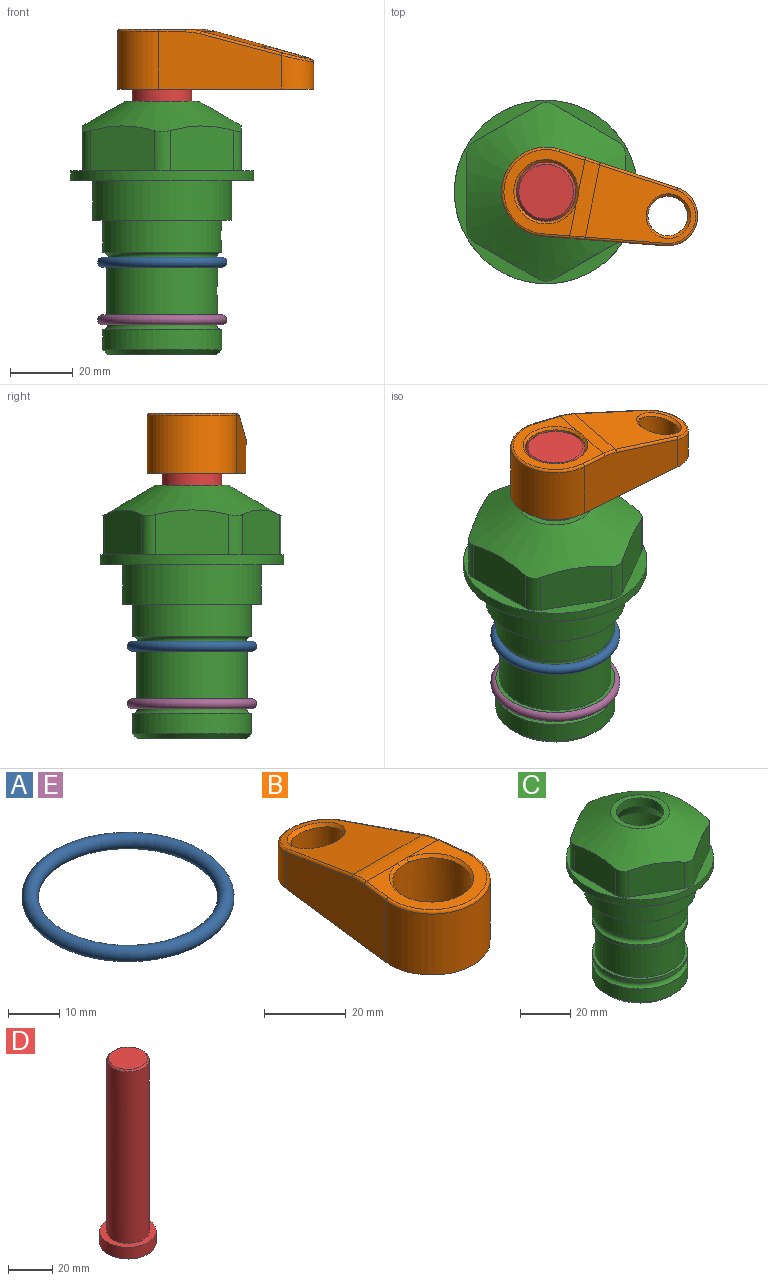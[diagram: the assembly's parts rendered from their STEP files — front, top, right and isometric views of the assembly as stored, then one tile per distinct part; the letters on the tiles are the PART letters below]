
ASSEMBLY  parts=5 mates=4
PART A: 1 faces, bbox 44.7x44.7x3.2 mm
  f0: torus R=19.05mm, axis (0,0,1), area 1193.9mm2
PART B: 31 faces, bbox 31.7x65.5x19.8 mm
  f0: plane 39.12x18.26mm, normal (0.99,0.12,0), area 612.2mm2, adj f1,f4,f7,f11,f13,f15
  f1: cylinder r=9.53mm len=18.91mm, axis (0,0,-1), area 296.1mm2, adj f0,f2,f7,f17
  f2: plane 39.12x18.26mm, normal (-0.99,0.12,0), area 612.2mm2, adj f1,f4,f7,f12,f14,f16
  f3: cylinder r=6.35mm len=12.7mm, axis (0,0,-1), area 362.4mm2, adj f7,f18
  f4: cylinder r=14.29mm len=28.58mm, axis (0,0,-1), area 882.2mm2, adj f0,f2,f7,f10
  f5: cylinder r=9.53mm len=19.05mm, axis (0,0,-1), area 1092.6mm2, adj f7,f19,f20
  f6: plane 26.99x23.69mm, normal (0,0,1), area 216.2mm2, adj f9,f10,f11,f12,f19
  f7: plane 63.5x28.58mm, normal (0,0,-1), area 661.8mm2, adj f0,f1,f2,f3,f4,f5,f22,f23
  f8: plane 33.52x23.6mm, normal (0,0.26,0.97), area 486mm2, adj f9,f15,f16,f17,f18
  f9: cylinder r=19.05mm len=24.72mm, axis (1,0,0), area 120.4mm2, adj f6,f8,f13,f14,f20
  f10: torus R=13.49mm, axis (0,0,1), area 59mm2, adj f4,f6,f11,f12
  f11: cylinder r=0.79mm len=8.67mm, axis (0.12,-0.99,0), area 10.8mm2, adj f0,f6,f10,f13
  f12: cylinder r=0.79mm len=8.67mm, axis (0.12,0.99,0), area 10.8mm2, adj f2,f6,f10,f14
  f13: bspline ~4.95x1.42mm, area 6.1mm2, adj f0,f9,f11,f15
  f14: bspline ~4.95x1.42mm, area 6.1mm2, adj f2,f9,f12,f16
  f15: cylinder r=0.79mm len=25.95mm, axis (0.12,-0.96,0.26), area 32.9mm2, adj f0,f8,f13,f17
  f16: cylinder r=0.79mm len=25.95mm, axis (0.12,0.96,-0.26), area 32.9mm2, adj f2,f8,f14,f17
  f17: bspline ~18.91x8.38mm, area 30mm2, adj f1,f8,f15,f16
  f18: bspline ~14.29x14.29mm, area 48.3mm2, adj f3,f8
  f19: cone r=9.53mm half-angle=45deg, axis (0,0,1), area 66.5mm2, adj f5,f6,f20
  f20: bspline ~3.22x0.96mm, area 3.5mm2, adj f5,f9,f19
  f21: plane 2.75x2.72mm, normal (0,0,-1), area 2.9mm2, adj f23,f25,f28
  f22: plane 23.05x15.88mm, normal (-0.99,-0.12,0), area 323.6mm2, adj f7,f25,f26,f27,f28,f29
  f23: plane 23.05x15.88mm, normal (0.99,-0.12,0), area 323.6mm2, adj f7,f21,f25,f27,f28,f30
  f24: cylinder r=9.53mm len=10.69mm, axis (0,0,-1), area 114.7mm2, adj f7,f27,f29,f30
  f25: cylinder r=12.7mm len=20.59mm, axis (0,0,-1), area 381.1mm2, adj f7,f21,f22,f23,f26,f28
  f26: plane 2.75x2.72mm, normal (0,0,-1), area 2.9mm2, adj f22,f25,f28
  f27: plane 19.72x18.37mm, normal (0,-0.26,-0.97), area 291.8mm2, adj f22,f23,f24,f28,f29,f30
  f28: cylinder r=15.88mm len=19.92mm, axis (1,0,0), area 54.8mm2, adj f21,f22,f23,f25,f26,f27
  f29: cylinder r=1.59mm len=11mm, axis (0,0,-1), area 34.7mm2, adj f7,f22,f24,f27
  f30: cylinder r=1.59mm len=11mm, axis (0,0,-1), area 34.7mm2, adj f7,f23,f24,f27
PART C: 36 faces, bbox 58.7x58.7x81 mm
  f0: cylinder r=17.78mm len=35.56mm, axis (0,0,1), area 1670.8mm2, adj f23,f24,f31
  f1: cylinder r=19.05mm len=38.1mm, axis (0,0,1), area 1191.9mm2, adj f26,f27,f30
  f2: plane 58.66x58.66mm, normal (0,0,-1), area 1150.6mm2, adj f3,f28
  f3: cylinder r=29.33mm len=58.66mm, axis (0,0,-1), area 585.1mm2, adj f2,f4
  f4: plane 58.66x58.66mm, normal (0,0,1), area 475.9mm2, adj f3,f5,f6,f7,f8,f9,f10,f11
  f5: plane 20.32x14.34mm, normal (-0.5,0.87,0), area 324.4mm2, adj f4,f15,f16,f17
  f6: plane 20.32x14.34mm, normal (0.5,0.87,0), area 324.4mm2, adj f4,f14,f15,f17
  f7: plane 23.48x14.34mm, normal (1,0,0), area 324.4mm2, adj f4,f13,f14,f17
  f8: plane 20.32x14.34mm, normal (0.5,-0.87,0), area 324.4mm2, adj f4,f12,f13,f17
  f9: plane 20.32x14.34mm, normal (-0.5,-0.87,0), area 324.4mm2, adj f4,f11,f12,f17
  f10: plane 23.48x14.34mm, normal (-1,0,0), area 324.4mm2, adj f4,f11,f16,f17
  f11: cylinder r=5.08mm len=12.85mm, axis (0,0,-1), area 67.2mm2, adj f4,f9,f10,f17
  f12: cylinder r=5.08mm len=12.85mm, axis (0,0,-1), area 67.2mm2, adj f4,f8,f9,f17
  f13: cylinder r=5.08mm len=12.85mm, axis (0,0,-1), area 67.2mm2, adj f4,f7,f8,f17
  f14: cylinder r=5.08mm len=12.85mm, axis (0,0,-1), area 67.2mm2, adj f4,f6,f7,f17
  f15: cylinder r=5.08mm len=12.85mm, axis (0,0,-1), area 67.2mm2, adj f4,f5,f6,f17
  f16: cylinder r=5.08mm len=12.85mm, axis (0,0,-1), area 67.2mm2, adj f4,f5,f10,f17
  f17: cone r=11.73mm half-angle=60deg, axis (0,0,-1), area 2071.8mm2, adj f5,f6,f7,f8,f9,f10,f11,f12
  f18: plane 23.46x23.46mm, normal (0,0,1), area 147.4mm2, adj f17,f35
  f19: plane 34.93x34.93mm, normal (0,0,-1), area 958mm2, adj f29
  f20: cylinder r=19.05mm len=38.1mm, axis (0,0,1), area 760.1mm2, adj f21,f29
  f21: torus R=19.05mm, axis (0,0,1), area 565.3mm2, adj f20,f22
  f22: cylinder r=19.05mm len=38.1mm, axis (0,0,1), area 190mm2, adj f21,f23
  f23: plane 38.1x38.1mm, normal (0,0,1), area 146.9mm2, adj f0,f22
  f24: plane 38.1x38.1mm, normal (0,0,-1), area 146.9mm2, adj f0,f25
  f25: cylinder r=19.05mm len=38.1mm, axis (0,0,1), area 190mm2, adj f24,f26
  f26: torus R=19.05mm, axis (0,0,1), area 565.3mm2, adj f1,f25
  f27: plane 44.45x44.45mm, normal (0,0,-1), area 411.7mm2, adj f1,f28
  f28: cylinder r=22.23mm len=44.45mm, axis (0,0,1), area 1773.5mm2, adj f2,f27
  f29: cone r=19.05mm half-angle=45deg, axis (0,0,1), area 257.5mm2, adj f19,f20
  f30: cylinder r=3.17mm len=6.75mm, axis (-1,0,0), area 128mm2, adj f1,f33
  f31: cylinder r=3.17mm len=6.35mm, axis (-1,0,0), area 102.5mm2, adj f0,f33
  f32: plane 25.4x25.4mm, normal (0,0,1), area 506.7mm2, adj f33
  f33: cylinder r=12.7mm len=66.42mm, axis (0,0,-1), area 5236.2mm2, adj f30,f31,f32,f34
  f34: cone r=9.53mm half-angle=30deg, axis (0,0,-1), area 443.4mm2, adj f33,f35
  f35: cylinder r=9.53mm len=19.05mm, axis (0,0,-1), area 240.9mm2, adj f18,f34
PART D: 6 faces, bbox 25.4x25.4x101.6 mm
  f0: plane 17.46x17.46mm, normal (0,0,1), area 239.5mm2, adj f5
  f1: plane 25.4x25.4mm, normal (0,0,-1), area 506.7mm2, adj f2
  f2: cylinder r=12.7mm len=25.4mm, axis (0,0,1), area 506.7mm2, adj f1,f3
  f3: plane 25.4x25.4mm, normal (0,0,1), area 221.7mm2, adj f2,f4
  f4: cylinder r=9.53mm len=94.46mm, axis (0,0,1), area 5653mm2, adj f3,f5
  f5: cone r=8.73mm half-angle=45deg, axis (0,0,-1), area 64.4mm2, adj f0,f4
PART E: same geometry as A
PLACE A t=(0,0,-1.59)mm
PLACE B rot(axis=(0,0,-1),101.3deg) t=(0,0,-15.14)mm
PLACE C at identity fixed
PLACE D rot(axis=(0,0,-1),101.3deg) t=(0,0,-15.94)mm
PLACE E t=(0,0,-20)mm
MATE fastened E.f0 <-> C.f0  axis (0,0,1) through (0,0,-44.51)mm
MATE fastened A.f0 <-> C.f0  axis (0,0,1) through (0,0,-26.1)mm
MATE cylindrical D.f2 <-> C.f0  axis (0,0,-1) through (0,0,-54.04)mm
MATE fastened B.f4 <-> D.f2  axis (0,0,-1) through (0,0,47.56)mm
